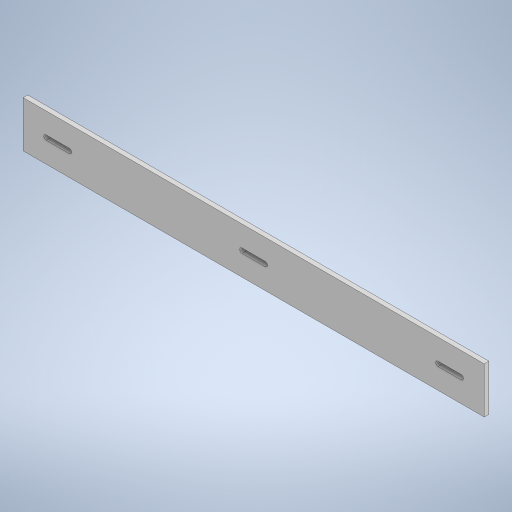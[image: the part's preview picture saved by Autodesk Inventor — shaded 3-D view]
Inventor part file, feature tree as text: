
AUTODESK INVENTOR PART (.ipt)
format: ipt  version: 2023 (Build 270158000, 158)  size: 245,248 bytes
history: native  units: mm
features: sketch x2, extrude x2
ambient origin geometry x8: Origin, YZ Plane, XZ Plane, XY Plane, X Axis, Y Axis, Z Axis, Center Point
bodies: Solid1 (feature_tree)
feature tree (4):
  sketch  "Sketch1"  dims[d0=1000.0mm d1=100.0mm]
  sketch  "Sketch2"  dims[d15=10.0mm d16=0.0mm d17=10.0mm d18=0.0mm]
  extrude  "Extrusion1"  Depth=100.0mm
  extrude  "Extrusion2"  Depth=10.0mm TaperAngle=0.0deg
